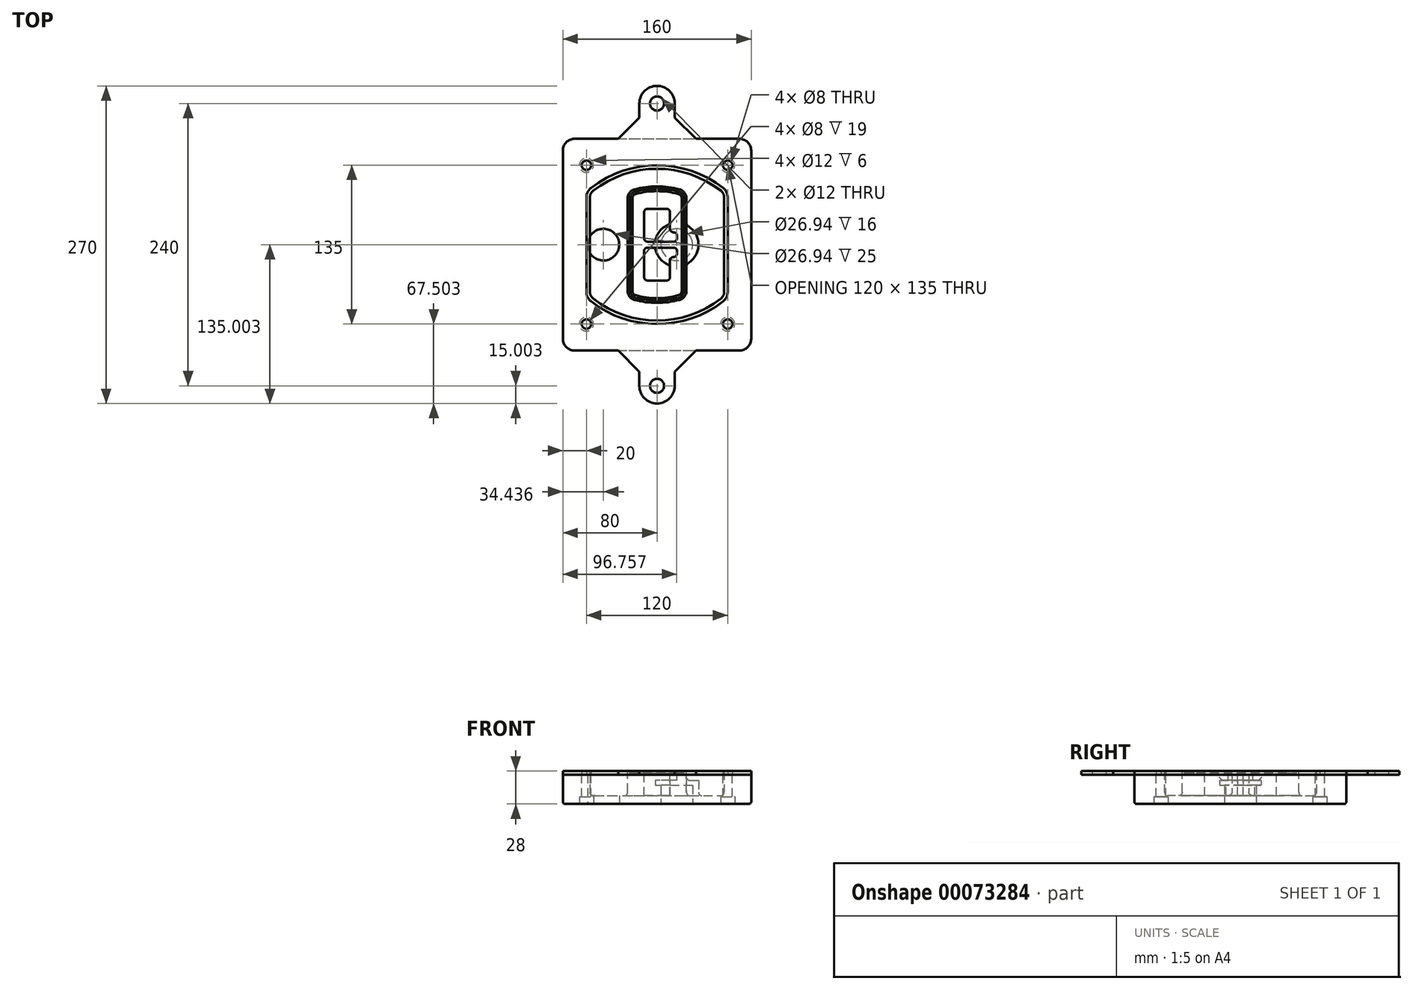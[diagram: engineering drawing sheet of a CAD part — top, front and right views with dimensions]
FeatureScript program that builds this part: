
annotation { "Feature Type Name" : "Feature", "Feature Type Description" : "" }
export const myFeature = defineFeature(function(context is Context, id is Id, definition is map)
    precondition{}
    {
        {
            var Q0;
            Q0=qCreatedBy(makeId("Top.planeOp"),FACE);
            var sketch = newSketch(context, id + "F0", { "sketchPlane" : qUnion([Q0])});
            skPoint(sketch, "E0.rect.middle", {"position": v(0, 0) * mm});
            skLineSegment(sketch, "E1.bottom", {"start": v(24.05, 28.38) * mm, "end": v(164.05, 28.38) * mm});
            skLineSegment(sketch, "E1.top", {"start": v(24.05, 208.38) * mm, "end": v(164.05, 208.38) * mm});
            skLineSegment(sketch, "E1.left", {"start": v(14.05, 38.38) * mm, "end": v(14.05, 198.38) * mm});
            skLineSegment(sketch, "E1.right", {"start": v(174.05, 38.38) * mm, "end": v(174.05, 198.38) * mm});
            skLineSegment(sketch, "E2", {"start": v(14.05, 208.38) * mm, "end": v(174.05, 28.38) * mm, "construction": true});
            skLineSegment(sketch, "E3", {"start": v(174.05, 208.38) * mm, "end": v(14.05, 28.38) * mm, "construction": true});
            skCircle(sketch, "E4", {"center": v(34.05, 185.88) * mm, "radius": 4 * mm});
            skCircle(sketch, "E5", {"center": v(154.05, 185.88) * mm, "radius": 4 * mm});
            skCircle(sketch, "E6", {"center": v(154.05, 50.88) * mm, "radius": 4 * mm});
            skCircle(sketch, "E7", {"center": v(34.05, 50.88) * mm, "radius": 4 * mm});
            skLineSegment(sketch, "E8", {"start": v(34.05, 185.88) * mm, "end": v(154.05, 185.88) * mm, "construction": true});
            skLineSegment(sketch, "E9", {"start": v(154.05, 185.88) * mm, "end": v(154.05, 50.88) * mm, "construction": true});
            skLineSegment(sketch, "E10", {"start": v(154.05, 50.88) * mm, "end": v(34.05, 50.88) * mm, "construction": true});
            skLineSegment(sketch, "E11", {"start": v(34.05, 50.88) * mm, "end": v(34.05, 185.88) * mm, "construction": true});
            skLineSegment(sketch, "E12", {"start": v(34.05, 158.68) * mm, "end": v(34.05, 78.09) * mm});
            skLineSegment(sketch, "E13", {"start": v(154.05, 158.68) * mm, "end": v(154.05, 78.09) * mm});
            skArc(sketch, "E14", {"start": v(150.2, 166.56) * mm, "mid": v(94.05, 185.88) * mm, "end": v(37.9, 166.56) * mm});
            skArc(sketch, "E15", {"start": v(37.9, 70.2) * mm, "mid": v(94.05, 50.88) * mm, "end": v(150.2, 70.2) * mm});
            skLineSegment(sketch, "E16", {"start": v(34.05, 118.38) * mm, "end": v(154.05, 118.38) * mm, "construction": true});
            skPoint(sketch, "E17.visualSharp", {"position": v(34.05, 73.38) * mm});
            skArc(sketch, "E17.filletArc", {"start": v(34.05, 78.09) * mm, "mid": v(35.06, 73.7) * mm, "end": v(37.9, 70.2) * mm});
            skPoint(sketch, "E18.visualSharp", {"position": v(34.05, 163.38) * mm});
            skArc(sketch, "E18.filletArc", {"start": v(37.9, 166.56) * mm, "mid": v(35.06, 163.06) * mm, "end": v(34.05, 158.68) * mm});
            skPoint(sketch, "E19.visualSharp", {"position": v(154.05, 163.38) * mm});
            skArc(sketch, "E19.filletArc", {"start": v(154.05, 158.68) * mm, "mid": v(153.04, 163.06) * mm, "end": v(150.2, 166.56) * mm});
            skPoint(sketch, "E20.visualSharp", {"position": v(154.05, 73.38) * mm});
            skArc(sketch, "E20.filletArc", {"start": v(150.2, 70.2) * mm, "mid": v(153.04, 73.7) * mm, "end": v(154.05, 78.09) * mm});
            skPoint(sketch, "E21.visualSharp", {"position": v(14.05, 208.38) * mm});
            skArc(sketch, "E21.filletArc", {"start": v(24.05, 208.38) * mm, "mid": v(16.98, 205.45) * mm, "end": v(14.05, 198.38) * mm});
            skPoint(sketch, "E22.visualSharp", {"position": v(174.05, 208.38) * mm});
            skArc(sketch, "E22.filletArc", {"start": v(174.05, 198.38) * mm, "mid": v(171.12, 205.45) * mm, "end": v(164.05, 208.38) * mm});
            skPoint(sketch, "E23.visualSharp", {"position": v(174.05, 28.38) * mm});
            skArc(sketch, "E23.filletArc", {"start": v(164.05, 28.38) * mm, "mid": v(171.12, 31.31) * mm, "end": v(174.05, 38.38) * mm});
            skPoint(sketch, "E24.visualSharp", {"position": v(14.05, 28.38) * mm});
            skArc(sketch, "E24.filletArc", {"start": v(14.05, 38.38) * mm, "mid": v(16.98, 31.31) * mm, "end": v(24.05, 28.38) * mm});
            skArc(sketch, "E25.0", {"start": v(151.05, 158.68) * mm, "mid": v(150.34, 161.75) * mm, "end": v(148.36, 164.2) * mm});
            skLineSegment(sketch, "E25.1", {"start": v(151.05, 158.68) * mm, "end": v(151.05, 78.09) * mm});
            skArc(sketch, "E25.2", {"start": v(148.36, 72.57) * mm, "mid": v(150.34, 75.02) * mm, "end": v(151.05, 78.09) * mm});
            skArc(sketch, "E25.3", {"start": v(39.74, 72.57) * mm, "mid": v(94.05, 53.88) * mm, "end": v(148.36, 72.57) * mm});
            skArc(sketch, "E25.4", {"start": v(37.05, 78.09) * mm, "mid": v(37.76, 75.02) * mm, "end": v(39.74, 72.57) * mm});
            skArc(sketch, "E25.5", {"start": v(148.36, 164.2) * mm, "mid": v(94.05, 182.88) * mm, "end": v(39.74, 164.2) * mm});
            skLineSegment(sketch, "E25.6", {"start": v(37.05, 158.68) * mm, "end": v(37.05, 78.09) * mm});
            skArc(sketch, "E25.7", {"start": v(39.74, 164.2) * mm, "mid": v(37.76, 161.75) * mm, "end": v(37.05, 158.68) * mm});
            skArc(sketch, "E26.0", {"start": v(35.43, 169.71) * mm, "mid": v(31.47, 164.82) * mm, "end": v(30.05, 158.68) * mm});
            skArc(sketch, "E26.1", {"start": v(152.67, 169.71) * mm, "mid": v(94.05, 189.88) * mm, "end": v(35.43, 169.71) * mm});
            skArc(sketch, "E26.2", {"start": v(158.05, 158.68) * mm, "mid": v(156.63, 164.82) * mm, "end": v(152.67, 169.71) * mm});
            skLineSegment(sketch, "E26.3", {"start": v(158.05, 158.68) * mm, "end": v(158.05, 78.09) * mm});
            skArc(sketch, "E26.4", {"start": v(152.67, 67.05) * mm, "mid": v(156.63, 71.95) * mm, "end": v(158.05, 78.09) * mm});
            skLineSegment(sketch, "E26.5", {"start": v(30.05, 158.68) * mm, "end": v(30.05, 78.09) * mm});
            skArc(sketch, "E26.6", {"start": v(35.43, 67.05) * mm, "mid": v(94.05, 46.88) * mm, "end": v(152.67, 67.05) * mm});
            skArc(sketch, "E26.7", {"start": v(30.05, 78.09) * mm, "mid": v(31.47, 71.95) * mm, "end": v(35.43, 67.05) * mm});
            skSolve(sketch);
        }
        {
            var Q0;
            Q0=makeQuery(id+"F0.imprint","IMPRINT",FACE,{"disambiguationData":[TD([[makeQuery(id+"F0.imprint","IMPRINT",EDGE,{"derivedFrom":sQuery(id+"F0.wireOp",EDGE,"E1.bottom")}),1.0]])]});
            var Q1;
            Q1=makeQuery(id+"F0.imprint","IMPRINT",FACE,{"disambiguationData":[TD([[makeQuery(id+"F0.imprint","IMPRINT",EDGE,{"derivedFrom":sQuery(id+"F0.wireOp",EDGE,"E12")}),1.0]])]});
            var Q2;
            Q2=makeQuery(id+"F0.imprint","IMPRINT",FACE,{"disambiguationData":[TD([[makeQuery(id+"F0.imprint","IMPRINT",EDGE,{"derivedFrom":sQuery(id+"F0.wireOp",EDGE,"E25.0")}),1.0]])]});
            var Q3;
            Q3=makeQuery(id+"F0.imprint","IMPRINT",FACE,{"disambiguationData":[TD([[makeQuery(id+"F0.imprint","IMPRINT",EDGE,{"derivedFrom":sQuery(id+"F0.wireOp",EDGE,"E12")}),-1.0]])]});
            extrude(context, id + "F1", {"entities" : qUnion([Q0, Q1, Q2, Q3]), "oppositeDirection" : true, "depth" : 25 * mm});
        }
        {
            var Q0;
            Q0=makeQuery(id+"F0.imprint","IMPRINT",FACE,{"disambiguationData":[TD([[makeQuery(id+"F0.imprint","IMPRINT",EDGE,{"derivedFrom":sQuery(id+"F0.wireOp",EDGE,"E12")}),1.0]])]});
            extrude(context, id + "F2", {"entities" : qUnion([Q0]), "operationType" : NewBodyOperationType.ADD, "depth" : 3 * mm});
        }
        {
            var Q0;
            Q0=makeQuery(id+"F0.imprint","IMPRINT",FACE,{"disambiguationData":[TD([[makeQuery(id+"F0.imprint","IMPRINT",EDGE,{"derivedFrom":sQuery(id+"F0.wireOp",EDGE,"E25.0")}),1.0]])]});
            extrude(context, id + "F3", {"entities" : qUnion([Q0]), "operationType" : NewBodyOperationType.REMOVE, "oppositeDirection" : true, "depth" : 18 * mm});
        }
        {
            var Q0;
            Q0=makeQuery(id+"F2.opExtrude","CAP_FACE",FACE,{"disambiguationData":[OSD([sQuery(id+"F0.wireOp",EDGE,"E12"),sQuery(id+"F0.wireOp",EDGE,"E13"),sQuery(id+"F0.wireOp",EDGE,"E14"),sQuery(id+"F0.wireOp",EDGE,"E15"),sQuery(id+"F0.wireOp",EDGE,"E17.filletArc"),sQuery(id+"F0.wireOp",EDGE,"E18.filletArc"),sQuery(id+"F0.wireOp",EDGE,"E19.filletArc"),sQuery(id+"F0.wireOp",EDGE,"E20.filletArc"),sQuery(id+"F0.wireOp",EDGE,"E25.0"),sQuery(id+"F0.wireOp",EDGE,"E25.1"),sQuery(id+"F0.wireOp",EDGE,"E25.2"),sQuery(id+"F0.wireOp",EDGE,"E25.3"),sQuery(id+"F0.wireOp",EDGE,"E25.4"),sQuery(id+"F0.wireOp",EDGE,"E25.5"),sQuery(id+"F0.wireOp",EDGE,"E25.6"),sQuery(id+"F0.wireOp",EDGE,"E25.7")])],"isStart":false});
            var sketch = newSketch(context, id + "F4", { "sketchPlane" : qUnion([Q0])});
            skArc(sketch, "E27.0", {"start": v(74.97, 71.41) * mm, "mid": v(94.05, 68.88) * mm, "end": v(113.13, 71.41) * mm});
            skArc(sketch, "E28.0", {"start": v(113.13, 165.35) * mm, "mid": v(94.05, 167.88) * mm, "end": v(74.97, 165.35) * mm});
            skLineSegment(sketch, "E29", {"start": v(69.05, 157.63) * mm, "end": v(69.05, 79.14) * mm});
            skLineSegment(sketch, "E30", {"start": v(119.05, 157.63) * mm, "end": v(119.05, 79.14) * mm});
            skLineSegment(sketch, "E31", {"start": v(69.05, 163.48) * mm, "end": v(119.05, 163.48) * mm, "construction": true});
            skLineSegment(sketch, "E32", {"start": v(69.05, 73.28) * mm, "end": v(119.05, 73.28) * mm, "construction": true});
            skPoint(sketch, "E33.visualSharp", {"position": v(69.05, 163.48) * mm});
            skArc(sketch, "E33.filletArc", {"start": v(74.97, 165.35) * mm, "mid": v(70.7, 162.5) * mm, "end": v(69.05, 157.63) * mm});
            skPoint(sketch, "E34.visualSharp", {"position": v(119.05, 163.48) * mm});
            skArc(sketch, "E34.filletArc", {"start": v(119.05, 157.63) * mm, "mid": v(117.4, 162.5) * mm, "end": v(113.13, 165.35) * mm});
            skPoint(sketch, "E35.visualSharp", {"position": v(119.05, 73.28) * mm});
            skArc(sketch, "E35.filletArc", {"start": v(113.13, 71.41) * mm, "mid": v(117.4, 74.27) * mm, "end": v(119.05, 79.14) * mm});
            skPoint(sketch, "E36.visualSharp", {"position": v(69.05, 73.28) * mm});
            skArc(sketch, "E36.filletArc", {"start": v(69.05, 79.14) * mm, "mid": v(70.7, 74.27) * mm, "end": v(74.97, 71.41) * mm});
            skArc(sketch, "E37.0", {"start": v(148.36, 164.2) * mm, "mid": v(94.05, 182.88) * mm, "end": v(39.74, 164.2) * mm});
            skArc(sketch, "E37.1", {"start": v(39.74, 164.2) * mm, "mid": v(37.76, 161.75) * mm, "end": v(37.05, 158.68) * mm});
            skLineSegment(sketch, "E37.2", {"start": v(37.05, 158.68) * mm, "end": v(37.05, 78.09) * mm});
            skArc(sketch, "E37.3", {"start": v(37.05, 78.09) * mm, "mid": v(37.76, 75.02) * mm, "end": v(39.74, 72.57) * mm});
            skArc(sketch, "E37.4", {"start": v(39.74, 72.57) * mm, "mid": v(94.05, 53.88) * mm, "end": v(148.36, 72.57) * mm});
            skArc(sketch, "E37.5", {"start": v(148.36, 72.57) * mm, "mid": v(150.34, 75.02) * mm, "end": v(151.05, 78.09) * mm});
            skLineSegment(sketch, "E37.6", {"start": v(151.05, 158.68) * mm, "end": v(151.05, 78.09) * mm});
            skArc(sketch, "E37.7", {"start": v(151.05, 158.68) * mm, "mid": v(150.34, 161.75) * mm, "end": v(148.36, 164.2) * mm});
            skLineSegment(sketch, "E38.0", {"start": v(117.05, 157.63) * mm, "end": v(117.05, 79.14) * mm});
            skArc(sketch, "E38.1", {"start": v(112.61, 73.34) * mm, "mid": v(115.81, 75.49) * mm, "end": v(117.05, 79.14) * mm});
            skArc(sketch, "E38.2", {"start": v(75.49, 73.34) * mm, "mid": v(94.05, 70.88) * mm, "end": v(112.61, 73.34) * mm});
            skArc(sketch, "E38.3", {"start": v(71.05, 79.14) * mm, "mid": v(72.29, 75.49) * mm, "end": v(75.49, 73.34) * mm});
            skLineSegment(sketch, "E38.4", {"start": v(71.05, 157.63) * mm, "end": v(71.05, 79.14) * mm});
            skArc(sketch, "E38.5", {"start": v(117.05, 157.63) * mm, "mid": v(115.81, 161.28) * mm, "end": v(112.61, 163.42) * mm});
            skArc(sketch, "E38.6", {"start": v(75.49, 163.42) * mm, "mid": v(72.29, 161.28) * mm, "end": v(71.05, 157.63) * mm});
            skArc(sketch, "E38.7", {"start": v(112.61, 163.42) * mm, "mid": v(94.05, 165.88) * mm, "end": v(75.49, 163.42) * mm});
            skArc(sketch, "E39.0", {"start": v(115.05, 157.63) * mm, "mid": v(114.23, 160.06) * mm, "end": v(112.1, 161.5) * mm});
            skLineSegment(sketch, "E39.1", {"start": v(115.05, 157.63) * mm, "end": v(115.05, 79.14) * mm});
            skArc(sketch, "E39.2", {"start": v(112.1, 75.27) * mm, "mid": v(114.23, 76.7) * mm, "end": v(115.05, 79.14) * mm});
            skArc(sketch, "E39.3", {"start": v(76, 75.27) * mm, "mid": v(94.05, 72.88) * mm, "end": v(112.1, 75.27) * mm});
            skArc(sketch, "E39.4", {"start": v(73.05, 79.14) * mm, "mid": v(73.87, 76.7) * mm, "end": v(76, 75.27) * mm});
            skArc(sketch, "E39.5", {"start": v(112.1, 161.5) * mm, "mid": v(94.05, 163.88) * mm, "end": v(76, 161.5) * mm});
            skLineSegment(sketch, "E39.6", {"start": v(73.05, 157.63) * mm, "end": v(73.05, 79.14) * mm});
            skArc(sketch, "E39.7", {"start": v(76, 161.5) * mm, "mid": v(73.87, 160.06) * mm, "end": v(73.05, 157.63) * mm});
            skLineSegment(sketch, "E40", {"start": v(69.05, 118.38) * mm, "end": v(119.05, 118.38) * mm, "construction": true});
            skLineSegment(sketch, "E41", {"start": v(83.05, 123.88) * mm, "end": v(83.05, 145.88) * mm});
            skLineSegment(sketch, "E42", {"start": v(86.05, 148.88) * mm, "end": v(102.05, 148.88) * mm});
            skLineSegment(sketch, "E43", {"start": v(105.05, 145.88) * mm, "end": v(105.05, 131.88) * mm});
            skLineSegment(sketch, "E44", {"start": v(108.05, 128.88) * mm, "end": v(108.05, 128.88) * mm});
            skLineSegment(sketch, "E45", {"start": v(111.05, 125.88) * mm, "end": v(111.05, 123.88) * mm});
            skLineSegment(sketch, "E46", {"start": v(108.05, 120.88) * mm, "end": v(86.05, 120.88) * mm});
            skPoint(sketch, "E47.visualSharp", {"position": v(83.05, 148.88) * mm});
            skArc(sketch, "E47.filletArc", {"start": v(86.05, 148.88) * mm, "mid": v(83.93, 148) * mm, "end": v(83.05, 145.88) * mm});
            skPoint(sketch, "E48.visualSharp", {"position": v(105.05, 148.88) * mm});
            skArc(sketch, "E48.filletArc", {"start": v(105.05, 145.88) * mm, "mid": v(104.17, 148) * mm, "end": v(102.05, 148.88) * mm});
            skPoint(sketch, "E49.visualSharp", {"position": v(105.05, 128.88) * mm});
            skArc(sketch, "E49.filletArc", {"start": v(105.05, 131.88) * mm, "mid": v(105.93, 129.76) * mm, "end": v(108.05, 128.88) * mm});
            skPoint(sketch, "E50.visualSharp", {"position": v(111.05, 128.88) * mm});
            skArc(sketch, "E50.filletArc", {"start": v(111.05, 125.88) * mm, "mid": v(110.17, 128) * mm, "end": v(108.05, 128.88) * mm});
            skPoint(sketch, "E51.visualSharp", {"position": v(111.05, 120.88) * mm});
            skArc(sketch, "E51.filletArc", {"start": v(108.05, 120.88) * mm, "mid": v(110.17, 121.76) * mm, "end": v(111.05, 123.88) * mm});
            skPoint(sketch, "E52.visualSharp", {"position": v(83.05, 120.88) * mm});
            skArc(sketch, "E52.filletArc", {"start": v(83.05, 123.88) * mm, "mid": v(83.93, 121.76) * mm, "end": v(86.05, 120.88) * mm});
            skLineSegment(sketch, "E53.0.MirrorCS", {"start": v(108.05, 115.88) * mm, "end": v(86.05, 115.88) * mm});
            skArc(sketch, "E54.0.MirrorCS", {"start": v(83.05, 112.88) * mm, "mid": v(83.93, 115) * mm, "end": v(86.05, 115.88) * mm});
            skLineSegment(sketch, "E55.0.MirrorCS", {"start": v(83.05, 112.88) * mm, "end": v(83.05, 90.88) * mm});
            skArc(sketch, "E56.0.MirrorCS", {"start": v(86.05, 87.88) * mm, "mid": v(83.93, 88.76) * mm, "end": v(83.05, 90.88) * mm});
            skLineSegment(sketch, "E57.0.MirrorCS", {"start": v(86.05, 87.88) * mm, "end": v(102.05, 87.88) * mm});
            skArc(sketch, "E58.0.MirrorCS", {"start": v(105.05, 90.88) * mm, "mid": v(104.17, 88.76) * mm, "end": v(102.05, 87.88) * mm});
            skLineSegment(sketch, "E59.0.MirrorCS", {"start": v(105.05, 90.88) * mm, "end": v(105.05, 104.88) * mm});
            skArc(sketch, "E60.0.MirrorCS", {"start": v(105.05, 104.88) * mm, "mid": v(105.93, 107) * mm, "end": v(108.05, 107.88) * mm});
            skArc(sketch, "E61.0.MirrorCS", {"start": v(111.05, 110.88) * mm, "mid": v(110.17, 108.76) * mm, "end": v(108.05, 107.88) * mm});
            skLineSegment(sketch, "E62.0.MirrorCS", {"start": v(111.05, 110.88) * mm, "end": v(111.05, 112.88) * mm});
            skArc(sketch, "E63.0.MirrorCS", {"start": v(108.05, 115.88) * mm, "mid": v(110.17, 115) * mm, "end": v(111.05, 112.88) * mm});
            skSolve(sketch);
        }
        {
            var Q0;
            Q0=makeQuery(id+"F4.imprint","IMPRINT",FACE,{"disambiguationData":[TD([[makeQuery(id+"F4.imprint","IMPRINT",EDGE,{"derivedFrom":sQuery(id+"F4.wireOp",EDGE,"E27.0")}),1.0]])]});
            var Q1;
            Q1=makeQuery(id+"F4.imprint","IMPRINT",FACE,{"disambiguationData":[TD([[makeQuery(id+"F4.imprint","IMPRINT",EDGE,{"derivedFrom":sQuery(id+"F4.wireOp",EDGE,"E38.0")}),-1.0]])]});
            var Q2;
            Q2=makeQuery(id+"F4.imprint","IMPRINT",FACE,{"disambiguationData":[TD([[makeQuery(id+"F4.imprint","IMPRINT",EDGE,{"derivedFrom":sQuery(id+"F4.wireOp",EDGE,"E39.0")}),1.0]])]});
            extrude(context, id + "F5", {"entities" : qUnion([Q0, Q1, Q2]), "operationType" : NewBodyOperationType.ADD, "endBound" : BoundingType.UP_TO_NEXT, "oppositeDirection" : true, "depth" : 25 * mm});
        }
        {
            var Q0;
            Q0=makeQuery(id+"F4.imprint","IMPRINT",FACE,{"disambiguationData":[TD([[makeQuery(id+"F4.imprint","IMPRINT",EDGE,{"derivedFrom":sQuery(id+"F4.wireOp",EDGE,"E38.0")}),-1.0]])]});
            extrude(context, id + "F6", {"entities" : qUnion([Q0]), "operationType" : NewBodyOperationType.REMOVE, "oppositeDirection" : true, "depth" : 2 * mm});
        }
        {
            var Q0;
            Q0=makeQuery(id+"F1.opExtrude","CAP_FACE",FACE,{"disambiguationData":[OSD([sQuery(id+"F0.wireOp",EDGE,"E1.bottom"),sQuery(id+"F0.wireOp",EDGE,"E1.top"),sQuery(id+"F0.wireOp",EDGE,"E1.left"),sQuery(id+"F0.wireOp",EDGE,"E1.right"),sQuery(id+"F0.wireOp",EDGE,"E4"),sQuery(id+"F0.wireOp",EDGE,"E5"),sQuery(id+"F0.wireOp",EDGE,"E6"),sQuery(id+"F0.wireOp",EDGE,"E7"),sQuery(id+"F0.wireOp",EDGE,"E21.filletArc"),sQuery(id+"F0.wireOp",EDGE,"E22.filletArc"),sQuery(id+"F0.wireOp",EDGE,"E23.filletArc"),sQuery(id+"F0.wireOp",EDGE,"E24.filletArc")])],"isStart":false});
            var sketch = newSketch(context, id + "F7", { "sketchPlane" : qUnion([Q0])});
            skCircle(sketch, "E64", {"center": v(110.8, -118.38) * mm, "radius": 13.47 * mm});
            skCircle(sketch, "E65", {"center": v(48.49, -118.38) * mm, "radius": 13.47 * mm});
            skLineSegment(sketch, "E66", {"start": v(174.05, -118.38) * mm, "end": v(14.05, -118.38) * mm});
            skCircle(sketch, "E67", {"center": v(110.8, -118.38) * mm, "radius": 18.47 * mm});
            skCircle(sketch, "E68", {"center": v(154.05, -185.88) * mm, "radius": 6 * mm});
            skCircle(sketch, "E69", {"center": v(34.05, -185.88) * mm, "radius": 6 * mm});
            skCircle(sketch, "E70", {"center": v(34.05, -50.88) * mm, "radius": 6 * mm});
            skCircle(sketch, "E71", {"center": v(154.05, -50.88) * mm, "radius": 6 * mm});
            skSolve(sketch);
        }
        {
            var Q0;
            {var subQ1=sQuery(id+"F7.wireOp",EDGE,"E66");var subQ4=sQuery(id+"F7.wireOp",EDGE,"E64");var subQ6=makeQuery(id+"F7.imprint","INTERSECT",VERTEX,{"disambiguationData":[OD(0.0)],"derivedFrom":[subQ4,subQ1]});Q0=makeQuery(id+"F7.imprint","IMPRINT",FACE,{"disambiguationData":[TD([[makeQuery(id+"F7.imprint","IMPRINT",EDGE,{"disambiguationData":[TD([[subQ6,-1.0]])],"derivedFrom":subQ4}),-1.0]])]});}
            var Q1;
            {var subQ0=sQuery(id+"F7.wireOp",EDGE,"E66");var subQ1=sQuery(id+"F7.wireOp",EDGE,"E64");var subQ3=makeQuery(id+"F7.imprint","INTERSECT",VERTEX,{"disambiguationData":[OD(0.0)],"derivedFrom":[subQ1,subQ0]});Q1=makeQuery(id+"F7.imprint","IMPRINT",FACE,{"disambiguationData":[TD([[makeQuery(id+"F7.imprint","IMPRINT",EDGE,{"disambiguationData":[TD([[subQ3,-1.0]])],"derivedFrom":subQ1}),1.0]])]});}
            var Q2;
            {var subQ0=sQuery(id+"F7.wireOp",EDGE,"E66");var subQ1=sQuery(id+"F7.wireOp",EDGE,"E64");var subQ3=makeQuery(id+"F7.imprint","INTERSECT",VERTEX,{"disambiguationData":[OD(0.0)],"derivedFrom":[subQ1,subQ0]});Q2=makeQuery(id+"F7.imprint","IMPRINT",FACE,{"disambiguationData":[TD([[makeQuery(id+"F7.imprint","IMPRINT",EDGE,{"disambiguationData":[TD([[subQ3,1.0]])],"derivedFrom":subQ1}),1.0]])]});}
            var Q3;
            {var subQ1=sQuery(id+"F7.wireOp",EDGE,"E66");var subQ4=sQuery(id+"F7.wireOp",EDGE,"E64");var subQ6=makeQuery(id+"F7.imprint","INTERSECT",VERTEX,{"disambiguationData":[OD(0.0)],"derivedFrom":[subQ4,subQ1]});Q3=makeQuery(id+"F7.imprint","IMPRINT",FACE,{"disambiguationData":[TD([[makeQuery(id+"F7.imprint","IMPRINT",EDGE,{"disambiguationData":[TD([[subQ6,1.0]])],"derivedFrom":subQ4}),-1.0]])]});}
            extrude(context, id + "F8", {"entities" : qUnion([Q0, Q1, Q2, Q3]), "operationType" : NewBodyOperationType.ADD, "oppositeDirection" : true, "depth" : 20 * mm});
        }
        {
            var Q0;
            {var subQ0=sQuery(id+"F7.wireOp",EDGE,"E66");var subQ1=sQuery(id+"F7.wireOp",EDGE,"E64");var subQ3=makeQuery(id+"F7.imprint","INTERSECT",VERTEX,{"disambiguationData":[OD(0.0)],"derivedFrom":[subQ1,subQ0]});Q0=makeQuery(id+"F7.imprint","IMPRINT",FACE,{"disambiguationData":[TD([[makeQuery(id+"F7.imprint","IMPRINT",EDGE,{"disambiguationData":[TD([[subQ3,-1.0]])],"derivedFrom":subQ1}),1.0]])]});}
            var Q1;
            {var subQ0=sQuery(id+"F7.wireOp",EDGE,"E66");var subQ1=sQuery(id+"F7.wireOp",EDGE,"E64");var subQ3=makeQuery(id+"F7.imprint","INTERSECT",VERTEX,{"disambiguationData":[OD(0.0)],"derivedFrom":[subQ1,subQ0]});Q1=makeQuery(id+"F7.imprint","IMPRINT",FACE,{"disambiguationData":[TD([[makeQuery(id+"F7.imprint","IMPRINT",EDGE,{"disambiguationData":[TD([[subQ3,1.0]])],"derivedFrom":subQ1}),1.0]])]});}
            extrude(context, id + "F9", {"entities" : qUnion([Q0, Q1]), "operationType" : NewBodyOperationType.REMOVE, "oppositeDirection" : true, "depth" : 16 * mm});
        }
        {
            var Q0;
            {var subQ0=sQuery(id+"F7.wireOp",EDGE,"E66");var subQ1=sQuery(id+"F7.wireOp",EDGE,"E65");var subQ3=makeQuery(id+"F7.imprint","INTERSECT",VERTEX,{"disambiguationData":[OD(0.0)],"derivedFrom":[subQ1,subQ0]});Q0=makeQuery(id+"F7.imprint","IMPRINT",FACE,{"disambiguationData":[TD([[makeQuery(id+"F7.imprint","IMPRINT",EDGE,{"disambiguationData":[TD([[subQ3,-1.0]])],"derivedFrom":subQ1}),1.0]])]});}
            var Q1;
            {var subQ0=sQuery(id+"F7.wireOp",EDGE,"E66");var subQ1=sQuery(id+"F7.wireOp",EDGE,"E65");var subQ3=makeQuery(id+"F7.imprint","INTERSECT",VERTEX,{"disambiguationData":[OD(0.0)],"derivedFrom":[subQ1,subQ0]});Q1=makeQuery(id+"F7.imprint","IMPRINT",FACE,{"disambiguationData":[TD([[makeQuery(id+"F7.imprint","IMPRINT",EDGE,{"disambiguationData":[TD([[subQ3,1.0]])],"derivedFrom":subQ1}),1.0]])]});}
            extrude(context, id + "F10", {"entities" : qUnion([Q0, Q1]), "operationType" : NewBodyOperationType.REMOVE, "oppositeDirection" : true, "depth" : 25 * mm});
        }
        {
            var Q0;
            Q0=makeQuery(id+"F7.imprint","IMPRINT",FACE,{"disambiguationData":[TD([[makeQuery(id+"F7.imprint","IMPRINT",EDGE,{"derivedFrom":sQuery(id+"F7.wireOp",EDGE,"E68")}),1.0]])]});
            var Q1;
            Q1=makeQuery(id+"F7.imprint","IMPRINT",FACE,{"disambiguationData":[TD([[makeQuery(id+"F7.imprint","IMPRINT",EDGE,{"derivedFrom":makeQuery(id+"F1.opExtrude","CAP_EDGE",EDGE,{"disambiguationData":[OSD([sQuery(id+"F0.wireOp",EDGE,"E5")])],"isStart":false})}),-1.0]])]});
            var Q2;
            Q2=makeQuery(id+"F7.imprint","IMPRINT",FACE,{"disambiguationData":[TD([[makeQuery(id+"F7.imprint","IMPRINT",EDGE,{"derivedFrom":sQuery(id+"F7.wireOp",EDGE,"E69")}),1.0]])]});
            var Q3;
            Q3=makeQuery(id+"F7.imprint","IMPRINT",FACE,{"disambiguationData":[TD([[makeQuery(id+"F7.imprint","IMPRINT",EDGE,{"derivedFrom":makeQuery(id+"F1.opExtrude","CAP_EDGE",EDGE,{"disambiguationData":[OSD([sQuery(id+"F0.wireOp",EDGE,"E4")])],"isStart":false})}),-1.0]])]});
            var Q4;
            Q4=makeQuery(id+"F7.imprint","IMPRINT",FACE,{"disambiguationData":[TD([[makeQuery(id+"F7.imprint","IMPRINT",EDGE,{"derivedFrom":sQuery(id+"F7.wireOp",EDGE,"E70")}),1.0]])]});
            var Q5;
            Q5=makeQuery(id+"F7.imprint","IMPRINT",FACE,{"disambiguationData":[TD([[makeQuery(id+"F7.imprint","IMPRINT",EDGE,{"derivedFrom":makeQuery(id+"F1.opExtrude","CAP_EDGE",EDGE,{"disambiguationData":[OSD([sQuery(id+"F0.wireOp",EDGE,"E7")])],"isStart":false})}),-1.0]])]});
            var Q6;
            Q6=makeQuery(id+"F7.imprint","IMPRINT",FACE,{"disambiguationData":[TD([[makeQuery(id+"F7.imprint","IMPRINT",EDGE,{"derivedFrom":sQuery(id+"F7.wireOp",EDGE,"E71")}),1.0]])]});
            var Q7;
            Q7=makeQuery(id+"F7.imprint","IMPRINT",FACE,{"disambiguationData":[TD([[makeQuery(id+"F7.imprint","IMPRINT",EDGE,{"derivedFrom":makeQuery(id+"F1.opExtrude","CAP_EDGE",EDGE,{"disambiguationData":[OSD([sQuery(id+"F0.wireOp",EDGE,"E6")])],"isStart":false})}),-1.0]])]});
            extrude(context, id + "F11", {"entities" : qUnion([Q0, Q1, Q2, Q3, Q4, Q5, Q6, Q7]), "operationType" : NewBodyOperationType.REMOVE, "oppositeDirection" : true, "depth" : 6 * mm});
        }
        {
            var Q0;
            Q0=makeQuery(id+"F9.boolean.opBoolean","COPY",FACE,{"derivedFrom":makeQuery(id+"F9.opExtrude","CAP_FACE",FACE,{"disambiguationData":[OSD([sQuery(id+"F7.wireOp",EDGE,"E64")])],"isStart":false})});
            var sketch = newSketch(context, id + "F12", { "sketchPlane" : qUnion([Q0])});
            skArc(sketch, "E72.0", {"start": v(105.05, -100.83) * mm, "mid": v(96.62, -106.56) * mm, "end": v(92.5, -115.88) * mm});
            skArc(sketch, "E72.1", {"start": v(92.5, -120.88) * mm, "mid": v(96.62, -130.2) * mm, "end": v(105.05, -135.93) * mm});
            skLineSegment(sketch, "E73", {"start": v(92.5, -120.88) * mm, "end": v(108.05, -120.88) * mm});
            skLineSegment(sketch, "E74.0", {"start": v(108.05, -115.88) * mm, "end": v(92.5, -115.88) * mm});
            skArc(sketch, "E74.1", {"start": v(108.05, -115.88) * mm, "mid": v(110.17, -115) * mm, "end": v(111.05, -112.88) * mm});
            skLineSegment(sketch, "E74.2", {"start": v(111.05, -110.88) * mm, "end": v(111.05, -112.88) * mm});
            skArc(sketch, "E74.3", {"start": v(111.05, -110.88) * mm, "mid": v(110.17, -108.76) * mm, "end": v(108.05, -107.88) * mm});
            skArc(sketch, "E74.4", {"start": v(105.05, -104.88) * mm, "mid": v(105.93, -107) * mm, "end": v(108.05, -107.88) * mm});
            skLineSegment(sketch, "E74.5", {"start": v(105.05, -100.83) * mm, "end": v(105.05, -104.88) * mm});
            skLineSegment(sketch, "E74.7", {"start": v(108.05, -120.88) * mm, "end": v(92.5, -120.88) * mm});
            skArc(sketch, "E74.8", {"start": v(108.05, -120.88) * mm, "mid": v(110.17, -121.76) * mm, "end": v(111.05, -123.88) * mm});
            skLineSegment(sketch, "E74.9", {"start": v(111.05, -125.88) * mm, "end": v(111.05, -123.88) * mm});
            skArc(sketch, "E74.10", {"start": v(111.05, -125.88) * mm, "mid": v(110.17, -128) * mm, "end": v(108.05, -128.88) * mm});
            skArc(sketch, "E74.11", {"start": v(105.05, -131.88) * mm, "mid": v(105.93, -129.76) * mm, "end": v(108.05, -128.88) * mm});
            skLineSegment(sketch, "E74.12", {"start": v(105.05, -135.93) * mm, "end": v(105.05, -131.88) * mm});
            skPoint(sketch, "E75.orphan", {"position": v(105.05, -145.88) * mm});
            skPoint(sketch, "E76.orphan", {"position": v(86.05, -120.88) * mm});
            skPoint(sketch, "E77.orphan", {"position": v(86.05, -115.88) * mm});
            skPoint(sketch, "E78.orphan", {"position": v(105.05, -90.88) * mm});
            skSolve(sketch);
        }
        {
            var Q0;
            {var subQ7=sQuery(id+"F12.wireOp",EDGE,"E72.0");var subQ14=sQuery(id+"F12.wireOp",EDGE,"E72.1");var subQ16=sQuery(id+"F12.wireOp",EDGE,"E74.1");var subQ18=sQuery(id+"F12.wireOp",EDGE,"E74.8");Q0=qUnion([makeQuery(id+"F12.imprint","IMPRINT",FACE,{"disambiguationData":[TD([[makeQuery(id+"F12.imprint","IMPRINT",EDGE,{"derivedFrom":subQ7}),1.0]])]}),makeQuery(id+"F12.imprint","IMPRINT",FACE,{"disambiguationData":[TD([[makeQuery(id+"F12.imprint","IMPRINT",EDGE,{"derivedFrom":subQ14}),1.0]])]}),makeQuery(id+"F12.imprint","IMPRINT",FACE,{"disambiguationData":[TD([[makeQuery(id+"F12.imprint","IMPRINT",EDGE,{"derivedFrom":subQ16}),1.0]])]}),makeQuery(id+"F12.imprint","IMPRINT",FACE,{"disambiguationData":[TD([[makeQuery(id+"F12.imprint","IMPRINT",EDGE,{"derivedFrom":subQ18}),-1.0]])]})]);}
            var Q1;
            Q1=makeQuery(id+"F5.boolean.opBoolean","SPLIT",FACE,{"disambiguationData":[TD([makeQuery(id+"F5.opExtrude","SWEPT_FACE",FACE,{"disambiguationData":[OSD([sQuery(id+"F4.wireOp",EDGE,"E41")])]})])],"derivedFrom":makeQuery(id+"F3.boolean.opBoolean","COPY",FACE,{"derivedFrom":makeQuery(id+"F3.opExtrude","CAP_FACE",FACE,{"disambiguationData":[OSD([sQuery(id+"F0.wireOp",EDGE,"E25.0"),sQuery(id+"F0.wireOp",EDGE,"E25.1"),sQuery(id+"F0.wireOp",EDGE,"E25.2"),sQuery(id+"F0.wireOp",EDGE,"E25.3"),sQuery(id+"F0.wireOp",EDGE,"E25.4"),sQuery(id+"F0.wireOp",EDGE,"E25.5"),sQuery(id+"F0.wireOp",EDGE,"E25.6"),sQuery(id+"F0.wireOp",EDGE,"E25.7")])],"isStart":false})})});
            extrude(context, id + "F13", {"entities" : qUnion([Q0]), "operationType" : NewBodyOperationType.REMOVE, "endBound" : BoundingType.UP_TO_SURFACE, "endBoundEntityFace" : qUnion([Q1]), "depth" : 25 * mm});
        }
        {
            var Q0;
            Q0=makeQuery(id+"F3.boolean.opBoolean","COPY",EDGE,{"derivedFrom":makeQuery(id+"F3.opExtrude","CAP_EDGE",EDGE,{"disambiguationData":[OSD([sQuery(id+"F0.wireOp",EDGE,"E25.6")])],"isStart":false})});
            var Q1;
            Q1=makeQuery(id+"F8.boolean.opBoolean","INTERSECT",EDGE,{"derivedFrom":[makeQuery(id+"F5.opExtrude","SWEPT_FACE",FACE,{"disambiguationData":[OSD([sQuery(id+"F4.wireOp",EDGE,"E30")])]}),makeQuery(id+"F8.opExtrude","CAP_FACE",FACE,{"disambiguationData":[OSD([sQuery(id+"F7.wireOp",EDGE,"E67")])],"isStart":false})]});
            var Q2;
            Q2=makeQuery(id+"F8.boolean.opBoolean","INTERSECT",EDGE,{"disambiguationData":[OD(1.0)],"derivedFrom":[makeQuery(id+"F5.opExtrude","SWEPT_FACE",FACE,{"disambiguationData":[OSD([sQuery(id+"F4.wireOp",EDGE,"E30")])]}),makeQuery(id+"F8.opExtrude","SWEPT_FACE",FACE,{"disambiguationData":[OSD([sQuery(id+"F7.wireOp",EDGE,"E67")])]})]});
            var Q3;
            {var subQ0=sQuery(id+"F4.wireOp",EDGE,"E30");Q3=makeQuery(id+"F8.boolean.opBoolean","SPLIT",EDGE,{"disambiguationData":[TD([makeQuery(id+"F5.opExtrude","SWEPT_FACE",FACE,{"disambiguationData":[OSD([sQuery(id+"F4.wireOp",EDGE,"E35.filletArc")])]})])],"derivedFrom":makeQuery(id+"F5.opExtrude","CAP_EDGE",EDGE,{"disambiguationData":[OSD([subQ0])],"isStart":false})});}
            var Q4;
            {var subQ0=sQuery(id+"F0.wireOp",EDGE,"E25.7");var subQ1=sQuery(id+"F0.wireOp",EDGE,"E25.1");var subQ2=sQuery(id+"F0.wireOp",EDGE,"E25.6");var subQ3=sQuery(id+"F0.wireOp",EDGE,"E25.5");var subQ4=sQuery(id+"F0.wireOp",EDGE,"E25.4");var subQ5=sQuery(id+"F0.wireOp",EDGE,"E25.0");var subQ6=sQuery(id+"F0.wireOp",EDGE,"E25.2");var subQ7=sQuery(id+"F0.wireOp",EDGE,"E25.3");Q4=makeQuery(id+"F8.boolean.opBoolean","INTERSECT",EDGE,{"derivedFrom":[makeQuery(id+"F5.boolean.opBoolean","SPLIT",FACE,{"disambiguationData":[TD([makeQuery(id+"F2.opExtrude","SWEPT_FACE",FACE,{"disambiguationData":[OSD([subQ5])]})])],"derivedFrom":makeQuery(id+"F3.boolean.opBoolean","COPY",FACE,{"derivedFrom":makeQuery(id+"F3.opExtrude","CAP_FACE",FACE,{"disambiguationData":[OSD([subQ5,subQ1,subQ6,subQ7,subQ4,subQ3,subQ2,subQ0])],"isStart":false})})}),makeQuery(id+"F8.opExtrude","SWEPT_FACE",FACE,{"disambiguationData":[OSD([sQuery(id+"F7.wireOp",EDGE,"E67")])]})]});}
            var Q5;
            Q5=makeQuery(id+"F8.boolean.opBoolean","INTERSECT",EDGE,{"disambiguationData":[OD(0.0)],"derivedFrom":[makeQuery(id+"F5.opExtrude","SWEPT_FACE",FACE,{"disambiguationData":[OSD([sQuery(id+"F4.wireOp",EDGE,"E30")])]}),makeQuery(id+"F8.opExtrude","SWEPT_FACE",FACE,{"disambiguationData":[OSD([sQuery(id+"F7.wireOp",EDGE,"E67")])]})]});
            fillet(context, id + "F14", {"entities" : qUnion([Q0, Q1, Q2, Q3, Q4, Q5]), "radius" : 3 * mm, "tangentPropagation" : true, "allowEdgeOverflow" : false});
        }
        {
            var Q0;
            Q0=makeQuery(id+"F1.opExtrude","CAP_EDGE",EDGE,{"disambiguationData":[OSD([sQuery(id+"F0.wireOp",EDGE,"E1.bottom")])],"isStart":false});
            fillet(context, id + "F15", {"entities" : qUnion([Q0]), "radius" : 2 * mm, "tangentPropagation" : true, "allowEdgeOverflow" : false});
        }
        {
            var Q0;
            {var subQ0=sQuery(id+"F0.wireOp",EDGE,"E22.filletArc");var subQ1=sQuery(id+"F0.wireOp",EDGE,"E7");var subQ2=sQuery(id+"F0.wireOp",EDGE,"E6");var subQ3=sQuery(id+"F0.wireOp",EDGE,"E5");var subQ4=sQuery(id+"F0.wireOp",EDGE,"E4");var subQ5=sQuery(id+"F0.wireOp",EDGE,"E1.bottom");var subQ6=sQuery(id+"F0.wireOp",EDGE,"E21.filletArc");var subQ7=sQuery(id+"F0.wireOp",EDGE,"E1.top");var subQ8=sQuery(id+"F0.wireOp",EDGE,"E1.left");var subQ9=sQuery(id+"F0.wireOp",EDGE,"E1.right");var subQ10=sQuery(id+"F0.wireOp",EDGE,"E23.filletArc");var subQ11=sQuery(id+"F0.wireOp",EDGE,"E24.filletArc");Q0=makeQuery(id+"F2.boolean.opBoolean","SPLIT",FACE,{"disambiguationData":[TD([makeQuery(id+"F1.opExtrude","SWEPT_FACE",FACE,{"disambiguationData":[OSD([subQ5])]})])],"derivedFrom":makeQuery(id+"F1.opExtrude","CAP_FACE",FACE,{"disambiguationData":[OSD([subQ5,subQ7,subQ8,subQ9,subQ4,subQ3,subQ2,subQ1,subQ6,subQ0,subQ10,subQ11])],"isStart":true})});}
            var sketch = newSketch(context, id + "F16", { "sketchPlane" : qUnion([Q0])});
            skCircle(sketch, "E79", {"center": v(94.05, 238.38) * mm, "radius": 6 * mm});
            skLineSegment(sketch, "E80", {"start": v(79.05, 226.38) * mm, "end": v(61.05, 208.38) * mm});
            skLineSegment(sketch, "E81", {"start": v(109.05, 226.38) * mm, "end": v(127.05, 208.38) * mm});
            skLineSegment(sketch, "E82", {"start": v(79.05, 226.38) * mm, "end": v(79.05, 238.38) * mm});
            skLineSegment(sketch, "E83", {"start": v(109.05, 226.38) * mm, "end": v(109.05, 238.38) * mm});
            skArc(sketch, "E84", {"start": v(109.05, 238.38) * mm, "mid": v(94.05, 253.38) * mm, "end": v(79.05, 238.38) * mm});
            skLineSegment(sketch, "E85", {"start": v(94.05, 238.38) * mm, "end": v(94.05, 208.38) * mm, "construction": true});
            skLineSegment(sketch, "E86", {"start": v(14.05, 118.38) * mm, "end": v(162.59, 118.38) * mm, "construction": true});
            skLineSegment(sketch, "E87.MirrorCS", {"start": v(79.05, 10.38) * mm, "end": v(61.05, 28.38) * mm});
            skLineSegment(sketch, "E88.MirrorCS", {"start": v(79.05, 10.38) * mm, "end": v(79.05, -1.62) * mm});
            skArc(sketch, "E89.MirrorCS", {"start": v(109.05, -1.62) * mm, "mid": v(94.05, -16.62) * mm, "end": v(79.05, -1.62) * mm});
            skCircle(sketch, "E90.MirrorC", {"center": v(94.05, -1.62) * mm, "radius": 6 * mm});
            skLineSegment(sketch, "E91.MirrorCS", {"start": v(109.05, 10.38) * mm, "end": v(109.05, -1.62) * mm});
            skLineSegment(sketch, "E92.MirrorCS", {"start": v(94.05, -1.62) * mm, "end": v(94.05, 28.38) * mm, "construction": true});
            skLineSegment(sketch, "E93.MirrorCS", {"start": v(109.05, 10.38) * mm, "end": v(127.05, 28.38) * mm});
            skSolve(sketch);
        }
        {
            var Q0;
            Q0=makeQuery(id+"F16.imprint","IMPRINT",FACE,{"disambiguationData":[TD([[makeQuery(id+"F16.imprint","IMPRINT",EDGE,{"derivedFrom":sQuery(id+"F16.wireOp",EDGE,"E79")}),-1.0]])]});
            var Q1;
            {var subQ0=sQuery(id+"F16.wireOp",EDGE,"E87.MirrorCS");Q1=makeQuery(id+"F16.imprint","IMPRINT",FACE,{"disambiguationData":[TD([[makeQuery(id+"F16.imprint","IMPRINT",EDGE,{"derivedFrom":subQ0}),-1.0]])]});}
            var Q2;
            Q2=makeQuery(id+"F16.imprint","IMPRINT",FACE,{"disambiguationData":[TD([[makeQuery(id+"F16.imprint","IMPRINT",EDGE,{"derivedFrom":makeQuery(id+"F1.opExtrude","CAP_EDGE",EDGE,{"disambiguationData":[OSD([sQuery(id+"F0.wireOp",EDGE,"E1.left")])],"isStart":true})}),-1.0]])]});
            var Q3;
            Q3=makeQuery(id+"F2.opExtrude","CAP_FACE",FACE,{"disambiguationData":[OSD([sQuery(id+"F0.wireOp",EDGE,"E12"),sQuery(id+"F0.wireOp",EDGE,"E13"),sQuery(id+"F0.wireOp",EDGE,"E14"),sQuery(id+"F0.wireOp",EDGE,"E15"),sQuery(id+"F0.wireOp",EDGE,"E17.filletArc"),sQuery(id+"F0.wireOp",EDGE,"E18.filletArc"),sQuery(id+"F0.wireOp",EDGE,"E19.filletArc"),sQuery(id+"F0.wireOp",EDGE,"E20.filletArc"),sQuery(id+"F0.wireOp",EDGE,"E25.0"),sQuery(id+"F0.wireOp",EDGE,"E25.1"),sQuery(id+"F0.wireOp",EDGE,"E25.2"),sQuery(id+"F0.wireOp",EDGE,"E25.3"),sQuery(id+"F0.wireOp",EDGE,"E25.4"),sQuery(id+"F0.wireOp",EDGE,"E25.5"),sQuery(id+"F0.wireOp",EDGE,"E25.6"),sQuery(id+"F0.wireOp",EDGE,"E25.7")])],"isStart":false});
            extrude(context, id + "F17", {"entities" : qUnion([Q0, Q1, Q2]), "endBound" : BoundingType.UP_TO_SURFACE, "endBoundEntityFace" : qUnion([Q3]), "depth" : 25 * mm});
        }
    });
